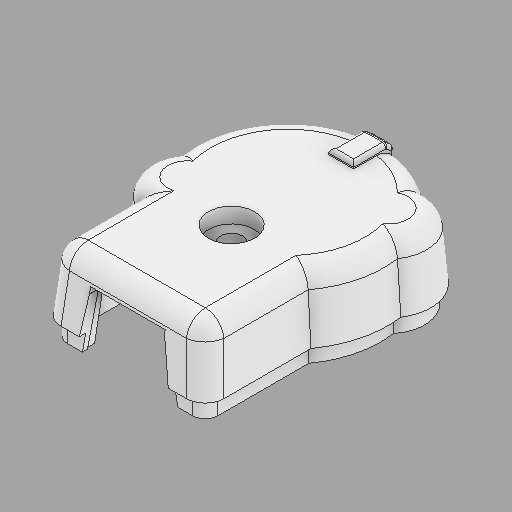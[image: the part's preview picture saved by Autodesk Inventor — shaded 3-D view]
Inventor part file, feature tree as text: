
AUTODESK INVENTOR PART (.ipt)
format: ipt  version: 2024.2 (Build 282272000, 272)  size: 300,544 bytes
history: native  units: in
note: dims shown in document units (in); Inventor stores cm internally (conversion verified against a paired STEP export)
features: fillet x1
ambient origin geometry x8: Origin, YZ Plane, XZ Plane, XY Plane, X Axis, Y Axis, Z Axis, Center Point
bodies: Solid1 (feature_tree)
feature tree (1):
  fillet  "Fillet18"  [1 undecoded]
note: 1 required parameter value undecoded (feature->parameter linkage not recoverable at this tier; creation-order binding heuristic only, values carry confidence <= 0.55)
